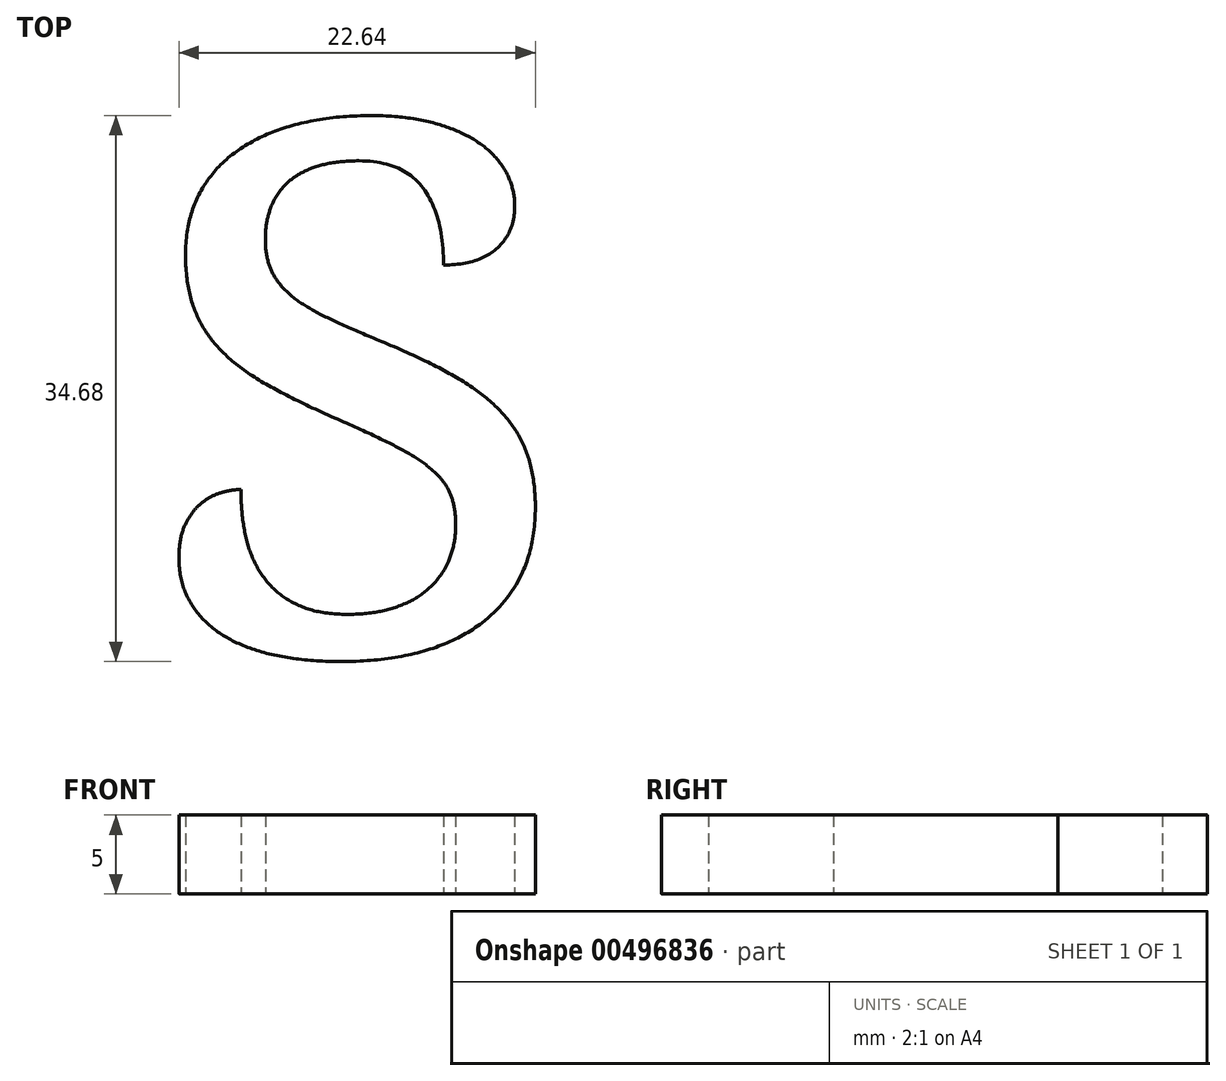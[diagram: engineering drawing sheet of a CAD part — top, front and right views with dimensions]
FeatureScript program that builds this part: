
annotation { "Feature Type Name" : "Feature", "Feature Type Description" : "" }
export const myFeature = defineFeature(function(context is Context, id is Id, definition is map)
    precondition{}
    {
        {
            var Q0;
            Q0=qCreatedBy(makeId("Top.planeOp"),FACE);
            var sketch = newSketch(context, id + "F0", { "sketchPlane" : qUnion([Q0])});
            skText(sketch, "E0", { "text": "s", "fontName": "NotoSerif-Regular.ttf"});
            const initialGuessF0  = {"E0": [-0.01687, -0.00929, 1, 0, 0.045]};
            skSetInitialGuess(sketch, initialGuessF0);
            skSolve(sketch);
        }
        {
            var Q0;
            Q0=qCreatedBy(makeId("Top.planeOp"),FACE);
            var sketch = newSketch(context, id + "F1", { "sketchPlane" : qUnion([Q0])});
            skSolve(sketch);
        }
        {
            var Q0;
            Q0 = qSketchRegion(id + "F1", true);
            var Q1;
            Q1=makeQuery(id+"F0.imprint","IMPRINT",FACE,{"disambiguationData":[TD([[makeQuery(id+"F0.imprint","IMPRINT",EDGE,{"derivedFrom":sQuery(id+"F0.wireOp",EDGE,"E0.sketch_text.stroke-0")}),-1.0]])]});
            extrude(context, id + "F2", {"entities" : qUnion([Q0, Q1]), "depth" : 5 * mm});
        }
    });
